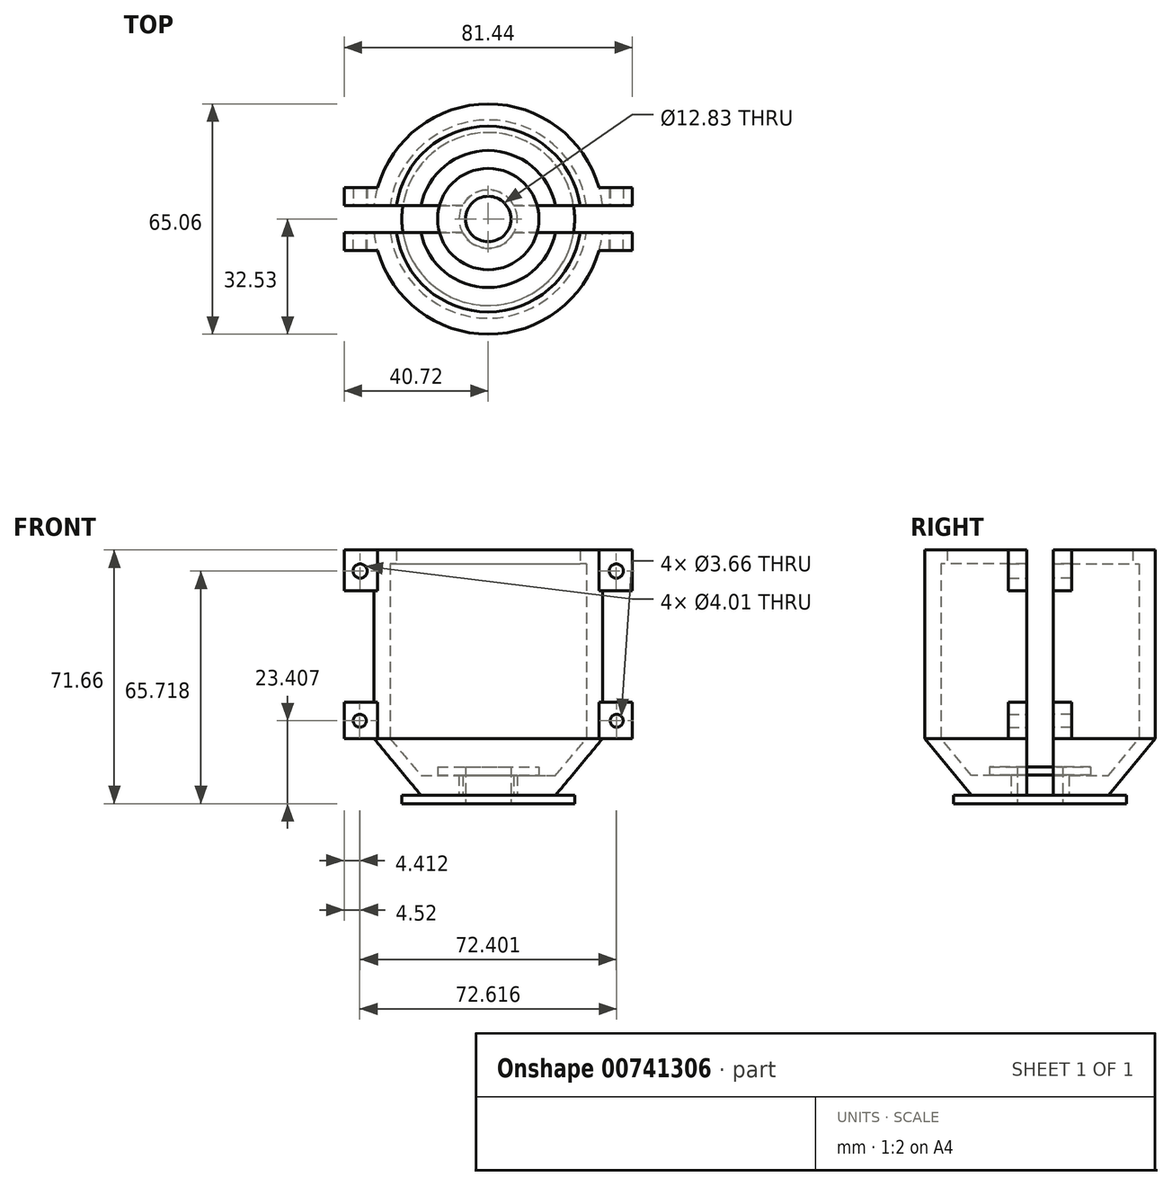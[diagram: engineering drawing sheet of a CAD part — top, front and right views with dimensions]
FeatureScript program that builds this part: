
annotation { "Feature Type Name" : "Feature", "Feature Type Description" : "" }
export const myFeature = defineFeature(function(context is Context, id is Id, definition is map)
    precondition{}
    {
        {
            var Q0;
            Q0=qCreatedBy(makeId("Front.planeOp"),FACE);
            var sketch = newSketch(context, id + "F0", { "sketchPlane" : qUnion([Q0])});
            skLineSegment(sketch, "E0", {"start": v(19.36, 0) * mm, "end": v(32.53, 16.02) * mm});
            skLineSegment(sketch, "E1", {"start": v(32.53, 16.02) * mm, "end": v(32.53, 69.3) * mm});
            skLineSegment(sketch, "E2", {"start": v(32.53, 69.3) * mm, "end": v(26.24, 69.3) * mm});
            skLineSegment(sketch, "E3", {"start": v(26.24, 69.3) * mm, "end": v(26.24, 65.36) * mm});
            skLineSegment(sketch, "E4", {"start": v(26.24, 65.36) * mm, "end": v(28.01, 65.36) * mm});
            skLineSegment(sketch, "E5", {"start": v(28.01, 65.36) * mm, "end": v(28.01, 16.02) * mm});
            skLineSegment(sketch, "E6", {"start": v(28.01, 16.02) * mm, "end": v(19.36, 5.6) * mm});
            skLineSegment(sketch, "E7", {"start": v(19.36, 5.6) * mm, "end": v(8.16, 5.6) * mm});
            skLineSegment(sketch, "E8", {"start": v(8.16, 5.6) * mm, "end": v(8.16, 0) * mm});
            skLineSegment(sketch, "E9", {"start": v(8.16, 0) * mm, "end": v(19.36, 0) * mm});
            skLineSegment(sketch, "E10", {"start": v(0, 0) * mm, "end": v(0, 63) * mm});
            skSolve(sketch);
        }
        {
            var Q0;
            Q0 = qSketchRegion(id + "F0", true);
            var Q1;
            Q1=sQuery(id+"F0.wireOp",EDGE,"E10");
            revolve(context, id + "F1", {"surfaceOperationType" : NewSurfaceOperationType.NEW, "entities" : qUnion([Q0]), "axis" : qUnion([Q1]), "revolveType" : RevolveType.FULL});
        }
        {
            var Q0;
            Q0=qCreatedBy(makeId("Front.planeOp"),FACE);
            var sketch = newSketch(context, id + "F2", { "sketchPlane" : qUnion([Q0])});
            skLineSegment(sketch, "E11.bottom", {"start": v(-38.24, 73.62) * mm, "end": v(44.13, 73.62) * mm});
            skLineSegment(sketch, "E11.top", {"start": v(-38.24, -11.9) * mm, "end": v(44.13, -11.9) * mm});
            skLineSegment(sketch, "E11.left", {"start": v(-38.24, 73.62) * mm, "end": v(-38.24, -11.9) * mm});
            skLineSegment(sketch, "E11.right", {"start": v(44.13, 73.62) * mm, "end": v(44.13, -11.9) * mm});
            skSolve(sketch);
        }
        {
            var Q0;
            Q0 = qSketchRegion(id + "F2", true);
            extrude(context, id + "F3", {"entities" : qUnion([Q0]), "operationType" : NewBodyOperationType.REMOVE, "endBound" : BoundingType.SYMMETRIC, "depth" : 7.62 * mm, "offsetDistance" : 25.4 * mm});
        }
        {
            var Q0;
            Q0=makeQuery(id+"F3.boolean.opBoolean","COPY",FACE,{"disambiguationData":[OD(1.0)],"derivedFrom":makeQuery(id+"F3.opExtrude","CAP_FACE",FACE,{"disambiguationData":[OSD([sQuery(id+"F2.wireOp",EDGE,"E11.bottom"),sQuery(id+"F2.wireOp",EDGE,"E11.top"),sQuery(id+"F2.wireOp",EDGE,"E11.left"),sQuery(id+"F2.wireOp",EDGE,"E11.right")])],"isStart":true})});
            var sketch = newSketch(context, id + "F4", { "sketchPlane" : qUnion([Q0])});
            skLineSegment(sketch, "E12.bottom", {"start": v(27.75, 16.02) * mm, "end": v(40.72, 16.02) * mm});
            skLineSegment(sketch, "E12.top", {"start": v(27.75, 26.32) * mm, "end": v(40.72, 26.32) * mm});
            skLineSegment(sketch, "E12.left", {"start": v(27.75, 16.02) * mm, "end": v(27.75, 26.32) * mm});
            skLineSegment(sketch, "E12.right", {"start": v(40.72, 16.02) * mm, "end": v(40.72, 26.32) * mm});
            skLineSegment(sketch, "E13.bottom", {"start": v(27.75, 69.3) * mm, "end": v(40.72, 69.3) * mm});
            skLineSegment(sketch, "E13.top", {"start": v(27.75, 57.76) * mm, "end": v(40.72, 57.76) * mm});
            skLineSegment(sketch, "E13.left", {"start": v(27.75, 69.3) * mm, "end": v(27.75, 57.76) * mm});
            skLineSegment(sketch, "E13.right", {"start": v(40.72, 69.3) * mm, "end": v(40.72, 57.76) * mm});
            skLineSegment(sketch, "E14.MirrorCS", {"start": v(-27.75, 69.3) * mm, "end": v(-40.72, 69.3) * mm});
            skLineSegment(sketch, "E15.MirrorCS", {"start": v(-27.75, 69.3) * mm, "end": v(-27.75, 57.76) * mm});
            skLineSegment(sketch, "E16.MirrorCS", {"start": v(-40.72, 69.3) * mm, "end": v(-40.72, 57.76) * mm});
            skLineSegment(sketch, "E17.MirrorCS", {"start": v(-27.75, 57.76) * mm, "end": v(-40.72, 57.76) * mm});
            skLineSegment(sketch, "E18.MirrorCS", {"start": v(-27.75, 26.32) * mm, "end": v(-40.72, 26.32) * mm});
            skLineSegment(sketch, "E19.MirrorCS", {"start": v(-27.75, 16.02) * mm, "end": v(-27.75, 26.32) * mm});
            skLineSegment(sketch, "E20.MirrorCS", {"start": v(-40.72, 16.02) * mm, "end": v(-40.72, 26.32) * mm});
            skLineSegment(sketch, "E21.MirrorCS", {"start": v(-27.75, 16.02) * mm, "end": v(-40.72, 16.02) * mm});
            skCircle(sketch, "E22", {"center": v(36.2, 63.36) * mm, "radius": 2 * mm});
            skCircle(sketch, "E23", {"center": v(36.3, 21.05) * mm, "radius": 1.83 * mm});
            skCircle(sketch, "E24.MirrorC", {"center": v(-36.2, 63.36) * mm, "radius": 2 * mm});
            skCircle(sketch, "E25.MirrorC", {"center": v(-36.3, 21.05) * mm, "radius": 1.83 * mm});
            skSolve(sketch);
        }
        {
            var Q0;
            Q0 = qSketchRegion(id + "F4", true);
            extrude(context, id + "F5", {"entities" : qUnion([Q0]), "operationType" : NewBodyOperationType.ADD, "oppositeDirection" : true, "depth" : 5.08 * mm, "offsetDistance" : 25.4 * mm});
        }
        {
            var Q0;
            Q0=makeQuery(id+"F3.boolean.opBoolean","SPLIT",BODY,{"disambiguationData":[OD(1.0)],"derivedFrom":makeQuery(id+"F1.opRevolve","SWEPT_BODY",BODY,{"disambiguationData":[OSD([sQuery(id+"F0.wireOp",EDGE,"E0"),sQuery(id+"F0.wireOp",EDGE,"E1"),sQuery(id+"F0.wireOp",EDGE,"E2"),sQuery(id+"F0.wireOp",EDGE,"E3"),sQuery(id+"F0.wireOp",EDGE,"E4"),sQuery(id+"F0.wireOp",EDGE,"E5"),sQuery(id+"F0.wireOp",EDGE,"E6"),sQuery(id+"F0.wireOp",EDGE,"E7"),sQuery(id+"F0.wireOp",EDGE,"E8"),sQuery(id+"F0.wireOp",EDGE,"E9")])]})});
            var Q1;
            Q1=qCreatedBy(makeId("Front.planeOp"),FACE);
            mirror(context, id + "F6", {"operationType" : NewBodyOperationType.ADD, "entities" : qUnion([Q0]), "mirrorPlane" : qUnion([Q1])});
        }
        {
            var Q0;
            Q0=qCreatedBy(makeId("Front.planeOp"),FACE);
            var sketch = newSketch(context, id + "F7", { "sketchPlane" : qUnion([Q0])});
            skLineSegment(sketch, "E26", {"start": v(8.25, 5.67) * mm, "end": v(14.32, 5.67) * mm});
            skLineSegment(sketch, "E27", {"start": v(14.32, 5.67) * mm, "end": v(14.32, 8.07) * mm});
            skLineSegment(sketch, "E28", {"start": v(14.32, 8.07) * mm, "end": v(6.42, 8.07) * mm});
            skLineSegment(sketch, "E29", {"start": v(6.42, 8.07) * mm, "end": v(6.42, -2.36) * mm});
            skLineSegment(sketch, "E30", {"start": v(6.42, -2.36) * mm, "end": v(24.43, -2.36) * mm});
            skLineSegment(sketch, "E31", {"start": v(24.43, -2.36) * mm, "end": v(24.43, 0) * mm});
            skLineSegment(sketch, "E32", {"start": v(24.43, 0) * mm, "end": v(8.25, 0) * mm});
            skLineSegment(sketch, "E33", {"start": v(8.25, 0) * mm, "end": v(8.25, 5.67) * mm});
            skSolve(sketch);
        }
        {
            var Q0;
            Q0 = qSketchRegion(id + "F7", true);
            var Q1;
            Q1=sQuery(id+"F0.wireOp",EDGE,"E10");
            revolve(context, id + "F8", {"surfaceOperationType" : NewSurfaceOperationType.NEW, "entities" : qUnion([Q0]), "axis" : qUnion([Q1]), "revolveType" : RevolveType.FULL});
        }
    });
